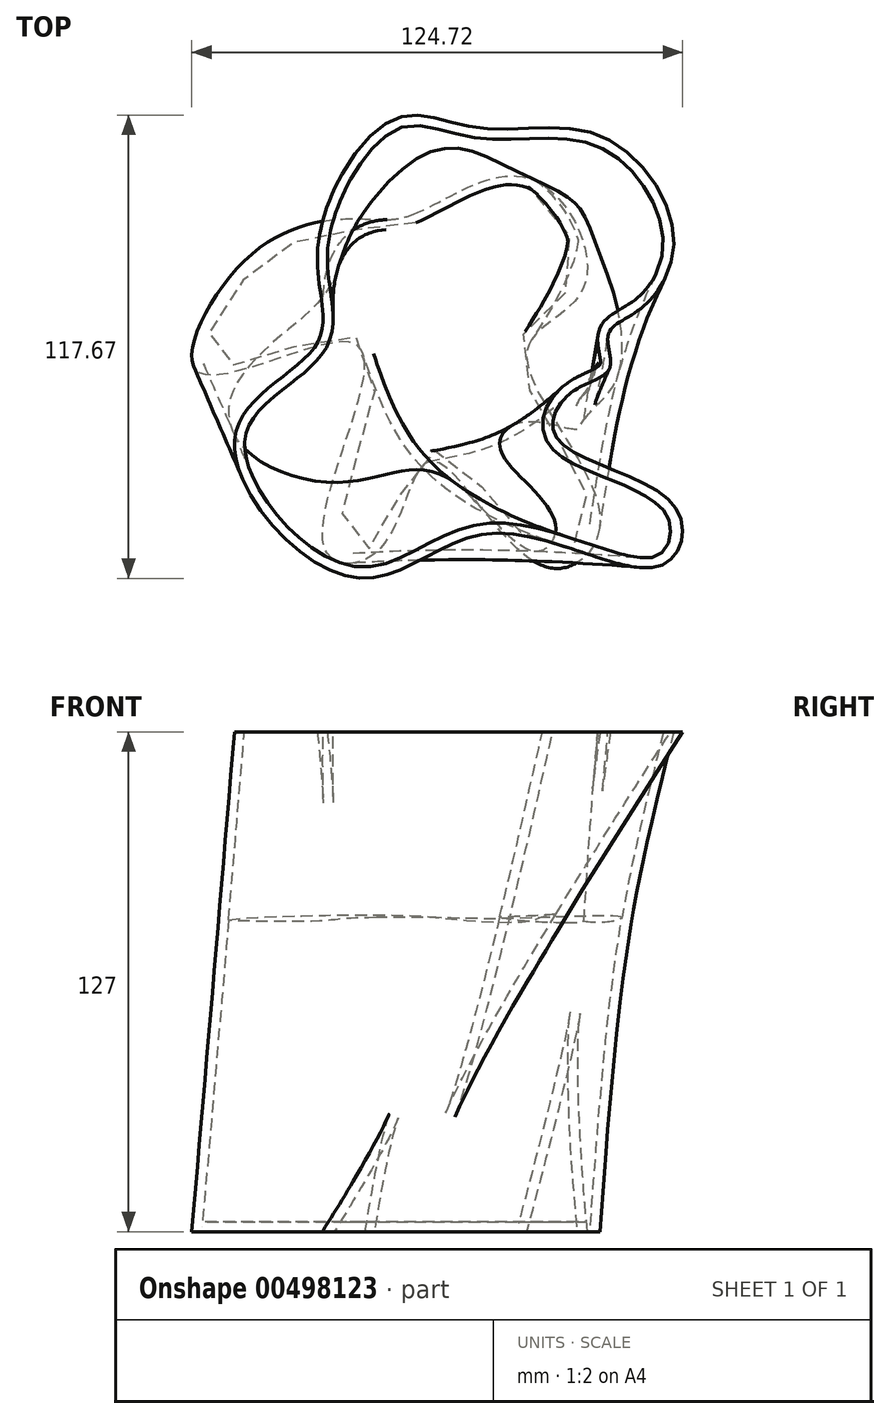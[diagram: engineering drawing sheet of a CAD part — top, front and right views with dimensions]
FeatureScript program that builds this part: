
annotation { "Feature Type Name" : "Feature", "Feature Type Description" : "" }
export const myFeature = defineFeature(function(context is Context, id is Id, definition is map)
    precondition{}
    {
        {
            var Q0;
            Q0=qCreatedBy(makeId("Top.planeOp"),FACE);
            var sketch = newSketch(context, id + "F0", { "sketchPlane" : qUnion([Q0])});
            skFitSpline(sketch, "E0", {"points": [v(-2.57, 34.94) * mm, v(26.81, 44.07) * mm, v(40.79, 16.69) * mm, v(26.24, 0) * mm, v(44.78, -41.79) * mm, v(32.23, -54.9) * mm, v(8.27, -31.8) * mm, v(0, -28.67) * mm, v(-11.7, -50.63) * mm, v(-24.53, -51.2) * mm, v(-17.4, -15.26) * mm, v(-18.83, 2.42) * mm, v(-57.05, -5.28) * mm, v(-44.5, 24.1) * mm, v(-16.54, 33.8) * mm, v(-2.57, 34.94) * mm]});
            skSolve(sketch);
        }
        {
            var Q0;
            Q0=qCreatedBy(makeId("Top.planeOp"),FACE);
            cPlane(context, id + "F1", {"entities" : qUnion([Q0]), "cplaneType" : CPlaneType.OFFSET, "offset" : 127 * mm, "width" : 152.4 * mm, "height" : 152.4 * mm});
        }
        {
            var Q0;
            Q0=qCreatedBy(id+"F1.planeOp",FACE);
            var sketch = newSketch(context, id + "F2", { "sketchPlane" : qUnion([Q0])});
            skFitSpline(sketch, "E1", {"points": [v(-7.54, 59.1) * mm, v(-26.88, 26.54) * mm, v(-27.12, 2.01) * mm, v(-47.9, -21.42) * mm, v(-18.17, -57.3) * mm, v(17.47, -46.11) * mm, v(60.27, -54.3) * mm, v(63.66, -39.18) * mm, v(33.97, -22.12) * mm, v(37.5, -10.35) * mm, v(47.24, -4.17) * mm, v(46.9, 4.35) * mm, v(54.63, 10.6) * mm, v(63.54, 28.7) * mm, v(45.52, 54.63) * mm, v(14.14, 56.86) * mm, v(-7.54, 59.1) * mm]});
            skSolve(sketch);
        }
        {
            var Q0;
            Q0=makeQuery(id+"F0.imprint","IMPRINT",FACE,{"disambiguationData":[TD([[makeQuery(id+"F0.imprint","IMPRINT",EDGE,{"derivedFrom":sQuery(id+"F0.wireOp",EDGE,"E0")}),-1.0]])]});
            var Q1;
            Q1=makeQuery(id+"F2.imprint","IMPRINT",FACE,{"disambiguationData":[TD([[makeQuery(id+"F2.imprint","IMPRINT",EDGE,{"derivedFrom":sQuery(id+"F2.wireOp",EDGE,"E1")}),1.0]])]});
            loft(context, id + "F3", {"sheetProfilesArray" : [{ "sheetProfileEntities" : qUnion([Q0]) }, { "sheetProfileEntities" : qUnion([Q1]) }]});
        }
        {
            var Q0;
            Q0=makeQuery(id+"F3.opLoft","CAP_FACE",FACE,{"disambiguationData":[OSD([makeQuery(id+"F2.imprint","IMPRINT",FACE,{"disambiguationData":[TD([[makeQuery(id+"F2.imprint","IMPRINT",EDGE,{"derivedFrom":sQuery(id+"F2.wireOp",EDGE,"E1")}),1.0]])]})])],"isStart":true});
            shell(context, id + "F4", {"entities" : qUnion([Q0]), "thickness" : 2.54 * mm});
        }
    });
